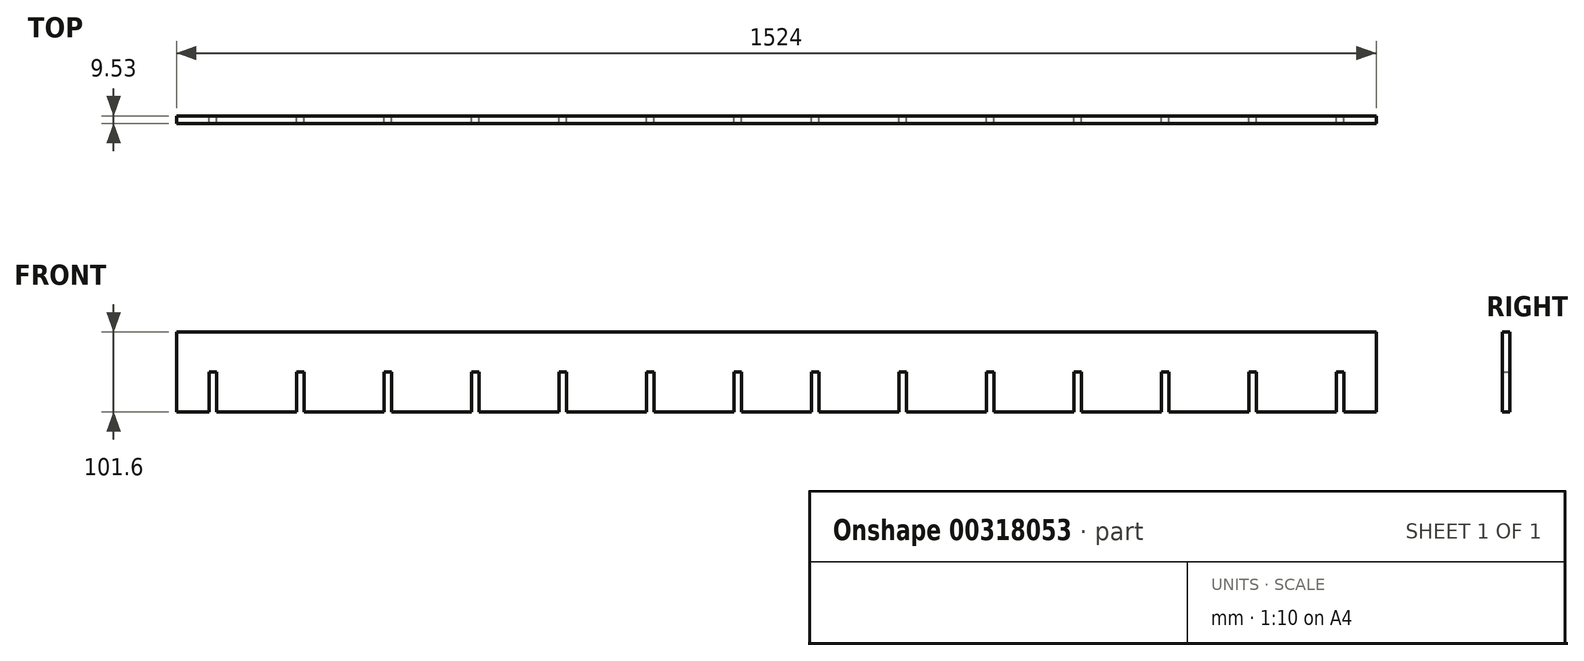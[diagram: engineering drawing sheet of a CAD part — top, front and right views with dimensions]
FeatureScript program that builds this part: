
annotation { "Feature Type Name" : "Feature", "Feature Type Description" : "" }
export const myFeature = defineFeature(function(context is Context, id is Id, definition is map)
    precondition{}
    {
        {
            var Q0;
            Q0=qCreatedBy(makeId("Right.planeOp"),FACE);
            var sketch = newSketch(context, id + "F0", { "sketchPlane" : qUnion([Q0])});
            skSolve(sketch);
        }
        {
            var Q0;
            Q0=qCreatedBy(makeId("Front.planeOp"),FACE);
            var sketch = newSketch(context, id + "F1", { "sketchPlane" : qUnion([Q0])});
            skLineSegment(sketch, "E0.bottom", {"start": v(-762, -50.8) * mm, "end": v(-720.73, -50.8) * mm});
            skLineSegment(sketch, "E0.top", {"start": v(-762, 50.8) * mm, "end": v(762, 50.8) * mm});
            skLineSegment(sketch, "E0.left", {"start": v(-762, -50.8) * mm, "end": v(-762, 50.8) * mm});
            skLineSegment(sketch, "E0.right", {"start": v(762, -50.8) * mm, "end": v(762, 50.8) * mm});
            skPoint(sketch, "E0.middle", {"position": v(0, 0) * mm});
            skLineSegment(sketch, "E1.top", {"start": v(-720.73, 0) * mm, "end": v(-711.2, 0) * mm});
            skLineSegment(sketch, "E1.left", {"start": v(-720.73, -50.8) * mm, "end": v(-720.73, 0) * mm});
            skLineSegment(sketch, "E1.right", {"start": v(-711.2, -50.8) * mm, "end": v(-711.2, 0) * mm});
            skLineSegment(sketch, "E2.top", {"start": v(-609.6, 0) * mm, "end": v(-600.08, 0) * mm});
            skLineSegment(sketch, "E2.left", {"start": v(-609.6, -50.8) * mm, "end": v(-609.6, 0) * mm});
            skLineSegment(sketch, "E2.right", {"start": v(-600.08, -50.8) * mm, "end": v(-600.08, 0) * mm});
            skLineSegment(sketch, "E3.trimOffspring", {"start": v(-711.2, -50.8) * mm, "end": v(-609.6, -50.8) * mm});
            skLineSegment(sketch, "E4.trimOffspring", {"start": v(-600.08, -50.8) * mm, "end": v(-498.48, -50.8) * mm});
            skLineSegment(sketch, "E5.top", {"start": v(-498.48, 0) * mm, "end": v(-488.95, 0) * mm});
            skLineSegment(sketch, "E5.left", {"start": v(-498.48, -50.8) * mm, "end": v(-498.48, 0) * mm});
            skLineSegment(sketch, "E5.right", {"start": v(-488.95, -50.8) * mm, "end": v(-488.95, 0) * mm});
            skLineSegment(sketch, "E6.top", {"start": v(-387.35, 0) * mm, "end": v(-377.82, 0) * mm});
            skLineSegment(sketch, "E6.left", {"start": v(-387.35, -50.8) * mm, "end": v(-387.35, 0) * mm});
            skLineSegment(sketch, "E6.right", {"start": v(-377.82, -50.8) * mm, "end": v(-377.82, 0) * mm});
            skLineSegment(sketch, "E7.top", {"start": v(-276.22, 0) * mm, "end": v(-266.7, 0) * mm});
            skLineSegment(sketch, "E7.left", {"start": v(-276.22, -50.8) * mm, "end": v(-276.22, 0) * mm});
            skLineSegment(sketch, "E7.right", {"start": v(-266.7, -50.8) * mm, "end": v(-266.7, 0) * mm});
            skLineSegment(sketch, "E8.trimOffspring", {"start": v(-488.95, -50.8) * mm, "end": v(-387.35, -50.8) * mm});
            skLineSegment(sketch, "E9.trimOffspring", {"start": v(-377.82, -50.8) * mm, "end": v(-276.22, -50.8) * mm});
            skLineSegment(sketch, "E10.trimOffspring", {"start": v(-266.7, -50.8) * mm, "end": v(-165.1, -50.8) * mm});
            skLineSegment(sketch, "E11.top", {"start": v(-165.1, 0) * mm, "end": v(-155.57, 0) * mm});
            skLineSegment(sketch, "E11.left", {"start": v(-165.1, -50.8) * mm, "end": v(-165.1, 0) * mm});
            skLineSegment(sketch, "E11.right", {"start": v(-155.57, -50.8) * mm, "end": v(-155.57, 0) * mm});
            skLineSegment(sketch, "E12.trimOffspring", {"start": v(-155.57, -50.8) * mm, "end": v(-53.97, -50.8) * mm});
            skLineSegment(sketch, "E13.top", {"start": v(-53.97, 0) * mm, "end": v(-44.45, 0) * mm});
            skLineSegment(sketch, "E13.left", {"start": v(-53.97, -50.8) * mm, "end": v(-53.97, 0) * mm});
            skLineSegment(sketch, "E13.right", {"start": v(-44.45, -50.8) * mm, "end": v(-44.45, 0) * mm});
            skLineSegment(sketch, "E14.trimOffspring", {"start": v(-44.45, -50.8) * mm, "end": v(44.45, -50.8) * mm});
            skLineSegment(sketch, "E15.top", {"start": v(44.45, 0) * mm, "end": v(53.97, 0) * mm});
            skLineSegment(sketch, "E15.left", {"start": v(44.45, -50.8) * mm, "end": v(44.45, 0) * mm});
            skLineSegment(sketch, "E15.right", {"start": v(53.98, -50.8) * mm, "end": v(53.97, 0) * mm});
            skLineSegment(sketch, "E16.trimOffspring", {"start": v(53.97, -50.8) * mm, "end": v(155.58, -50.8) * mm});
            skLineSegment(sketch, "E17.top", {"start": v(155.58, 0) * mm, "end": v(165.1, 0) * mm});
            skLineSegment(sketch, "E17.left", {"start": v(155.58, -50.8) * mm, "end": v(155.58, 0) * mm});
            skLineSegment(sketch, "E17.right", {"start": v(165.1, -50.8) * mm, "end": v(165.1, 0) * mm});
            skLineSegment(sketch, "E18.trimOffspring", {"start": v(165.1, -50.8) * mm, "end": v(266.7, -50.8) * mm});
            skLineSegment(sketch, "E19.top", {"start": v(266.7, 0) * mm, "end": v(276.23, 0) * mm});
            skLineSegment(sketch, "E19.left", {"start": v(266.7, -50.8) * mm, "end": v(266.7, 0) * mm});
            skLineSegment(sketch, "E19.right", {"start": v(276.23, -50.8) * mm, "end": v(276.23, 0) * mm});
            skLineSegment(sketch, "E20.trimOffspring", {"start": v(276.23, -50.8) * mm, "end": v(377.82, -50.8) * mm});
            skLineSegment(sketch, "E21.top", {"start": v(377.83, 0) * mm, "end": v(387.35, 0) * mm});
            skLineSegment(sketch, "E21.left", {"start": v(377.83, -50.8) * mm, "end": v(377.83, 0) * mm});
            skLineSegment(sketch, "E21.right", {"start": v(387.35, -50.8) * mm, "end": v(387.35, 0) * mm});
            skLineSegment(sketch, "E22.trimOffspring", {"start": v(387.35, -50.8) * mm, "end": v(488.95, -50.8) * mm});
            skLineSegment(sketch, "E23.top", {"start": v(488.95, 0) * mm, "end": v(498.48, 0) * mm});
            skLineSegment(sketch, "E23.left", {"start": v(488.95, -50.8) * mm, "end": v(488.95, 0) * mm});
            skLineSegment(sketch, "E23.right", {"start": v(498.48, -50.8) * mm, "end": v(498.48, 0) * mm});
            skLineSegment(sketch, "E24.trimOffspring", {"start": v(498.48, -50.8) * mm, "end": v(600.08, -50.8) * mm});
            skLineSegment(sketch, "E25.top", {"start": v(600.08, 0) * mm, "end": v(609.6, 0) * mm});
            skLineSegment(sketch, "E25.left", {"start": v(600.08, -50.8) * mm, "end": v(600.08, 0) * mm});
            skLineSegment(sketch, "E25.right", {"start": v(609.6, -50.8) * mm, "end": v(609.6, 0) * mm});
            skLineSegment(sketch, "E26.trimOffspring", {"start": v(609.6, -50.8) * mm, "end": v(711.2, -50.8) * mm});
            skLineSegment(sketch, "E27.top", {"start": v(711.2, 0) * mm, "end": v(720.73, 0) * mm});
            skLineSegment(sketch, "E27.left", {"start": v(711.2, -50.8) * mm, "end": v(711.2, 0) * mm});
            skLineSegment(sketch, "E27.right", {"start": v(720.73, -50.8) * mm, "end": v(720.73, 0) * mm});
            skLineSegment(sketch, "E28.trimOffspring", {"start": v(720.73, -50.8) * mm, "end": v(762, -50.8) * mm});
            skSolve(sketch);
        }
        {
            var Q0;
            Q0 = qSketchRegion(id + "F1", true);
            var Q1;
            Q1 = qSketchRegion(id + "F0", true);
            extrude(context, id + "F2", {"entities" : qUnion([Q0, Q1]), "depth" : 9.52 * mm});
        }
    });
